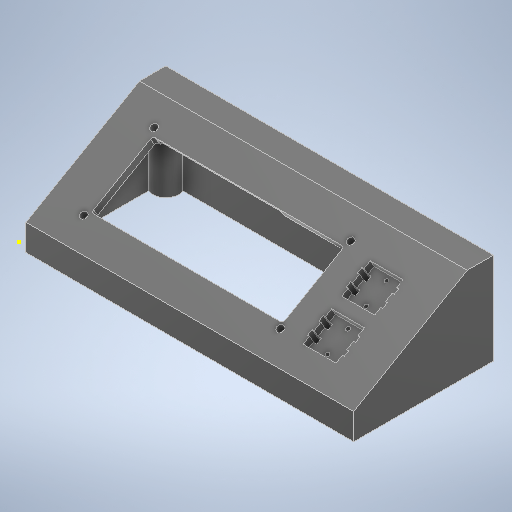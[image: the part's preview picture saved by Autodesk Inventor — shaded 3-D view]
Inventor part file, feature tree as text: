
AUTODESK INVENTOR PART (.ipt)
format: ipt  version: 2025.1 (Build 291241020, 241B)  size: 1,132,032 bytes
history: native  units: mm
features: sketch x16, extrude x11, projected_geometry x9, plane x6, hole x2, mirror x2, shell x1, fillet x1
ambient origin geometry x8: Origin, YZ Plane, XZ Plane, XY Plane, X Axis, Y Axis, Z Axis, Center Point
bodies: Solid1 (feature_tree)
feature tree (48):
  extrude  "Extrusion1"  TaperAngle=30.0deg  [1 undecoded]
  shell  "Shell1"  Thickness=10.0mm
  extrude  "Extrusion2"  Depth=3.0mm
  plane  "Work Plane1"
  plane  "Work Plane2"
  hole  "Hole1"  [1 undecoded]
  extrude  "Extrusion3"  Depth=11.5mm
  sketch  "Sketch5"  dims[d12=120.0mm d13=0.0mm d14=75.0mm]
  plane  "Work Plane3"
  plane  "Work Plane4"
  extrude  "Extrusion4"  Depth=75.0mm
  extrude  "Extrusion5"  Depth=37.0mm
  sketch  "Sketch9"  dims[d17=15.8mm]
  sketch  "Sketch10"  dims[d18=2.6mm d19=6.0mm d20=4.0mm d21=2.0mm d22=90.0deg d23=8.0mm d24=0.0mm d25=15.0mm]
  extrude  "Extrusion6"  Depth=15.0mm
  plane  "Work Plane5"
  mirror  "Mirror1"
  extrude  "Extrusion7"  Depth=10.0mm TaperAngle=0.0deg
  extrude  "Extrusion8"  Depth=12.0mm
  hole  "Hole2"  [1 undecoded]
  plane  "Work Plane6"
  mirror  "Mirror2"
  extrude  "Extrusion9"  Depth=6.0mm
  extrude  "Extrusion10"  Depth=1.0mm
  sketch  "Sketch17"  dims[d42=4.5mm]
  fillet  "Fillet1"  Radius=7.0mm
  extrude  "Extrusion11"  Depth=1.45mm
  sketch  "Sketch1"  dims[d0=10.0mm d2=30.0deg d3=10.0mm]
  sketch  "Sketch2"  dims[d4=125.0mm d5=0.0mm d6=3.0mm]
  sketch  "Sketch3"  dims[d7=50.0mm d8=27.0mm]
  sketch  "Sketch4"  dims[d9=73.0mm d11=11.5mm]
  sketch  "Sketch8"  dims[d15=31.0mm d16=37.0mm]
  sketch  "Sketch11"  dims[d26=3.0mm d27=0.0mm d28=10.0mm d29=0.0mm]
  sketch  "Sketch12"  dims[d30=2.0mm d31=0.0mm d32=12.0mm]
  sketch  "Sketch13"  dims[d33=12.0mm d34=7.0mm]
  sketch  "Sketch14"  dims[d35=6.0mm d36=6.0mm]
  sketch  "Sketch15"  dims[d37=1.0mm d38=1.0mm d39=7.0mm]
  sketch  "Sketch16"  dims[d40=1.45mm d41=1.45mm]
  projected_geometry  "Projected Loop1"
  projected_geometry  "Projected Loop2"
  projected_geometry  "Projected Loop3"
  projected_geometry  "Projected Loop4"
  projected_geometry  "Projected Loop5"
  projected_geometry  "Projected Loop6"
  projected_geometry  "Projected Loop7"
  projected_geometry  "Projected Loop8"
  sketch  "Sketch18"  dims[d43=4.5mm d44=2.7mm d45=2.0mm d46=0.5mm d47=135.0deg d48=1.992893mm d49=0.5mm d50=10.0mm d51=10.0mm d52=6.0mm d53=135.0deg d54=1.0mm d55=0.5mm d56=1.0mm d57=12.0mm d58=0.5mm d59=6.0mm d60=10.0mm d62=10.0mm d64=1.0mm d65=2.0mm d66=2.5mm d67=1.0mm d68=2.0mm d69=2.5mm d70=1.0mm d71=1.0mm d72=10.0mm d73=10.0mm d74=0.0mm d75=0.0mm d76=20.0mm d78=6.0mm d79=6.0mm d80=4.0mm d81=2.0mm d82=2.0mm d83=10.0mm d84=5.0mm d85=5.0mm d86=3.0mm d87=0.0mm d88=10.0mm d89=5.0mm d90=5.0mm d91=10.0mm d92=0.0mm d95=4.8mm d96=6.0mm d97=4.0mm d98=2.0mm d99=90.0deg d100=8.0mm d101=0.0mm d102=12.5mm d103=9.75mm d104=0.25mm d105=2.25mm d106=3.0mm d107=0.0mm d108=3.0mm d109=0.0mm d110=1.0mm d113=3.5mm d115=3.0mm d116=50.0mm d117=2.0mm d118=0.0mm]
  projected_geometry  "Projected Loop9"
note: 3 required parameter values undecoded (feature->parameter linkage not recoverable at this tier; creation-order binding heuristic only, values carry confidence <= 0.55)
